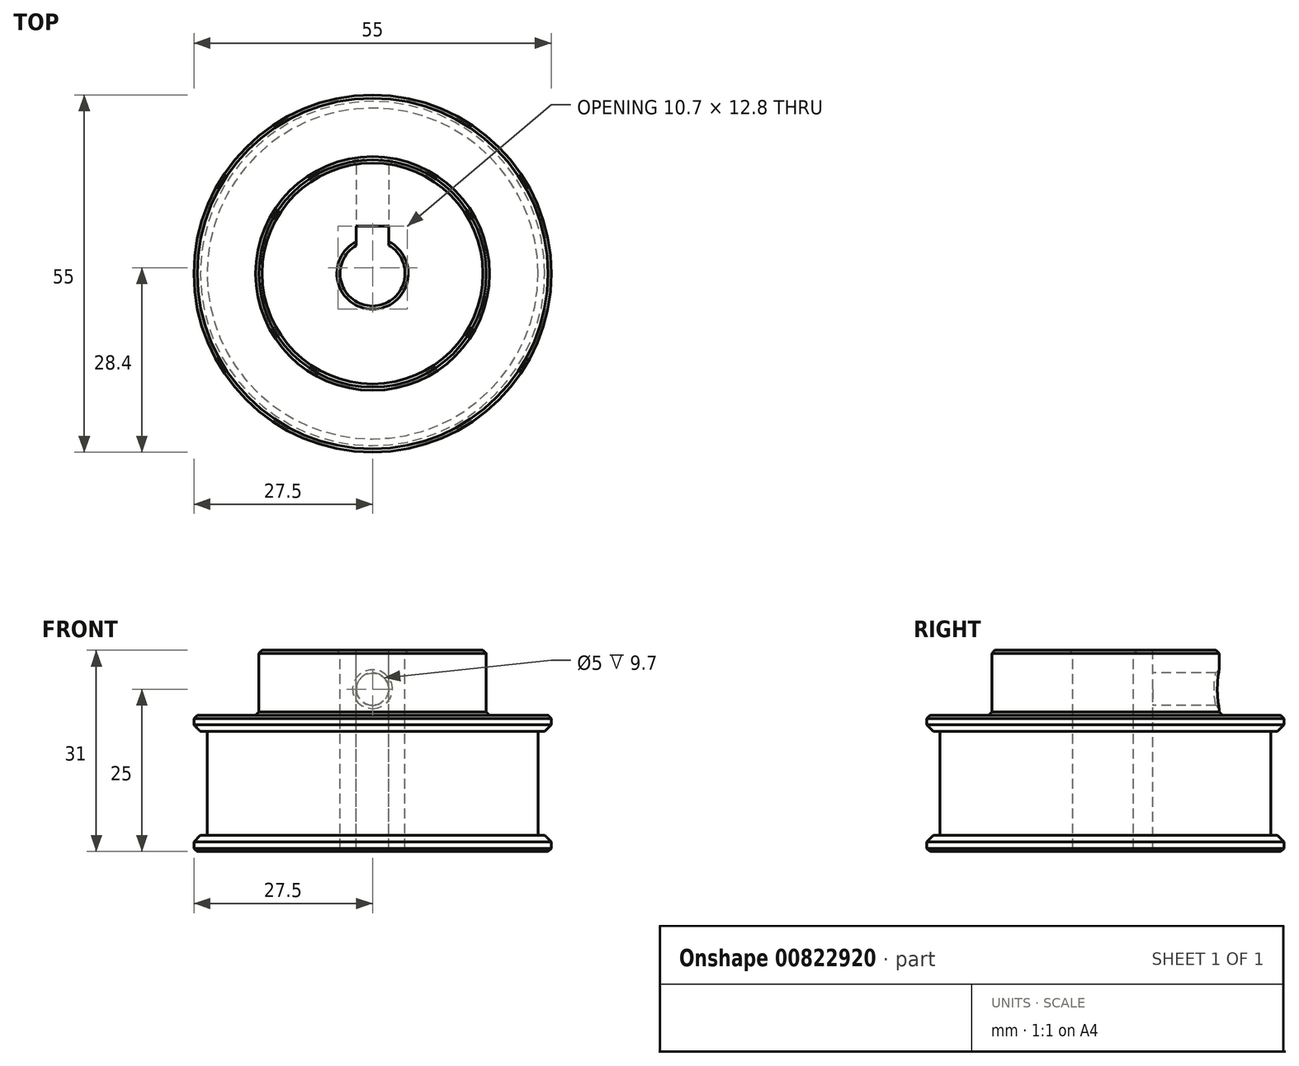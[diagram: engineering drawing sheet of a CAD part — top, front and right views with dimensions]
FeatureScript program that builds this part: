
annotation { "Feature Type Name" : "Feature", "Feature Type Description" : "" }
export const myFeature = defineFeature(function(context is Context, id is Id, definition is map)
    precondition{}
    {
        {
            var Q0;
            Q0=qCreatedBy(makeId("Front.planeOp"),FACE);
            var sketch = newSketch(context, id + "F0", { "sketchPlane" : qUnion([Q0])});
            skLineSegment(sketch, "E0", {"start": v(0, 38.23) * mm, "end": v(0, 0) * mm, "construction": true});
            skLineSegment(sketch, "E1", {"start": v(0, 0) * mm, "end": v(-5, 0) * mm, "construction": true});
            skLineSegment(sketch, "E2", {"start": v(-5, 0) * mm, "end": v(-5, 31) * mm});
            skLineSegment(sketch, "E3", {"start": v(-5, 31) * mm, "end": v(-17.5, 31) * mm});
            skLineSegment(sketch, "E4", {"start": v(-17.5, 31) * mm, "end": v(-17.5, 21) * mm});
            skLineSegment(sketch, "E5", {"start": v(-17.5, 21) * mm, "end": v(-27.5, 21) * mm});
            skLineSegment(sketch, "E6", {"start": v(-27.5, 21) * mm, "end": v(-27.5, 18.5) * mm});
            skLineSegment(sketch, "E7", {"start": v(-27.5, 18.5) * mm, "end": v(-25.46, 18.5) * mm});
            skLineSegment(sketch, "E8", {"start": v(-25.46, 18.5) * mm, "end": v(-25.46, 2.5) * mm});
            skLineSegment(sketch, "E9", {"start": v(-25.46, 2.5) * mm, "end": v(-27.5, 2.5) * mm});
            skLineSegment(sketch, "E10", {"start": v(-27.5, 2.5) * mm, "end": v(-27.5, 0) * mm});
            skLineSegment(sketch, "E11", {"start": v(-27.5, 0) * mm, "end": v(-5, 0) * mm});
            skSolve(sketch);
        }
        {
            var Q0;
            Q0=qSketchRegion(id+"F0",true);
            var Q1;
            Q1=sQuery(id+"F0.wireOp",EDGE,"E0");
            revolve(context, id + "F1", {"surfaceOperationType" : NewSurfaceOperationType.NEW, "entities" : qUnion([Q0]), "axis" : qUnion([Q1]), "revolveType" : RevolveType.FULL});
        }
        {
            var Q0;
            Q0=makeQuery(id+"F1.opRevolve","SWEPT_EDGE",EDGE,{"disambiguationData":[OSD([sQuery(id+"F0.wireOp",EDGE,"E9"),sQuery(id+"F0.wireOp",EDGE,"E10")])]});
            var Q1;
            Q1=makeQuery(id+"F1.opRevolve","SWEPT_EDGE",EDGE,{"disambiguationData":[OSD([sQuery(id+"F0.wireOp",EDGE,"E6"),sQuery(id+"F0.wireOp",EDGE,"E7")])]});
            chamfer(context, id + "F2", {"entities" : qUnion([Q0, Q1]), "width" : 1 * mm, "tangentPropagation" : true});
        }
        {
            var Q0;
            Q0=makeQuery(id+"F1.opRevolve","SWEPT_FACE",FACE,{"disambiguationData":[OSD([sQuery(id+"F0.wireOp",EDGE,"E5")])]});
            var Q1;
            Q1=makeQuery(id+"F1.opRevolve","SWEPT_FACE",FACE,{"disambiguationData":[OSD([sQuery(id+"F0.wireOp",EDGE,"E3")])]});
            var Q2;
            Q2=makeQuery(id+"F1.opRevolve","SWEPT_FACE",FACE,{"disambiguationData":[OSD([sQuery(id+"F0.wireOp",EDGE,"E11")])]});
            chamfer(context, id + "F3", {"entities" : qUnion([Q0, Q1, Q2]), "width" : 0.5 * mm, "tangentPropagation" : true});
        }
        {
            var Q0;
            Q0=makeQuery(id+"F1.opRevolve","SWEPT_FACE",FACE,{"disambiguationData":[OSD([sQuery(id+"F0.wireOp",EDGE,"E3")])]});
            var sketch = newSketch(context, id + "F4", { "sketchPlane" : qUnion([Q0])});
            skLineSegment(sketch, "E12", {"start": v(0, 0) * mm, "end": v(0, 4.8) * mm, "construction": true});
            skLineSegment(sketch, "E13.bottom", {"start": v(-2.5, 2.3) * mm, "end": v(2.5, 2.3) * mm});
            skLineSegment(sketch, "E13.top", {"start": v(-2.5, 7.3) * mm, "end": v(2.5, 7.3) * mm});
            skLineSegment(sketch, "E13.left", {"start": v(-2.5, 2.3) * mm, "end": v(-2.5, 7.3) * mm});
            skLineSegment(sketch, "E13.right", {"start": v(2.5, 2.3) * mm, "end": v(2.5, 7.3) * mm});
            skPoint(sketch, "E13.middle", {"position": v(0, 4.8) * mm});
            skCircle(sketch, "E14.0", {"center": v(0, 0) * mm, "radius": 5 * mm, "construction": true});
            skPoint(sketch, "E15", {"position": v(0, -5) * mm});
            skSolve(sketch);
        }
        {
            var Q0;
            Q0=qSketchRegion(id+"F4",true);
            var Q1;
            Q1=makeQuery(id+"F1.opRevolve","SWEPT_FACE",FACE,{"disambiguationData":[OSD([sQuery(id+"F0.wireOp",EDGE,"E11")])]});
            extrude(context, id + "F5", {"entities" : qUnion([Q0]), "operationType" : NewBodyOperationType.REMOVE, "endBound" : BoundingType.UP_TO_SURFACE, "oppositeDirection" : true, "depth" : 25 * mm, "endBoundEntityFace" : qUnion([Q1]), "offsetDistance" : 25 * mm});
        }
        {
            var Q0;
            Q0=qCreatedBy(makeId("Front.planeOp"),FACE);
            var sketch = newSketch(context, id + "F6", { "sketchPlane" : qUnion([Q0])});
            skLineSegment(sketch, "E16", {"start": v(0, 0) * mm, "end": v(0, 25) * mm, "construction": true});
            skCircle(sketch, "E17", {"center": v(0, 25) * mm, "radius": 2.5 * mm});
            skSolve(sketch);
        }
        {
            var Q0;
            Q0=qSketchRegion(id+"F6",true);
            extrude(context, id + "F7", {"entities" : qUnion([Q0]), "operationType" : NewBodyOperationType.REMOVE, "oppositeDirection" : true, "depth" : 25 * mm, "offsetDistance" : 25 * mm});
        }
        {
            var Q0;
            Q0=makeQuery(id+"F7.boolean.opBoolean","INTERSECT",EDGE,{"derivedFrom":[makeQuery(id+"F1.opRevolve","SWEPT_FACE",FACE,{"disambiguationData":[OSD([sQuery(id+"F0.wireOp",EDGE,"E4")])]}),makeQuery(id+"F7.opExtrude","SWEPT_FACE",FACE,{"disambiguationData":[OSD([sQuery(id+"F6.wireOp",EDGE,"E17")])]})]});
            chamfer(context, id + "F8", {"entities" : qUnion([Q0]), "width" : 0.5 * mm, "tangentPropagation" : true});
        }
    });
